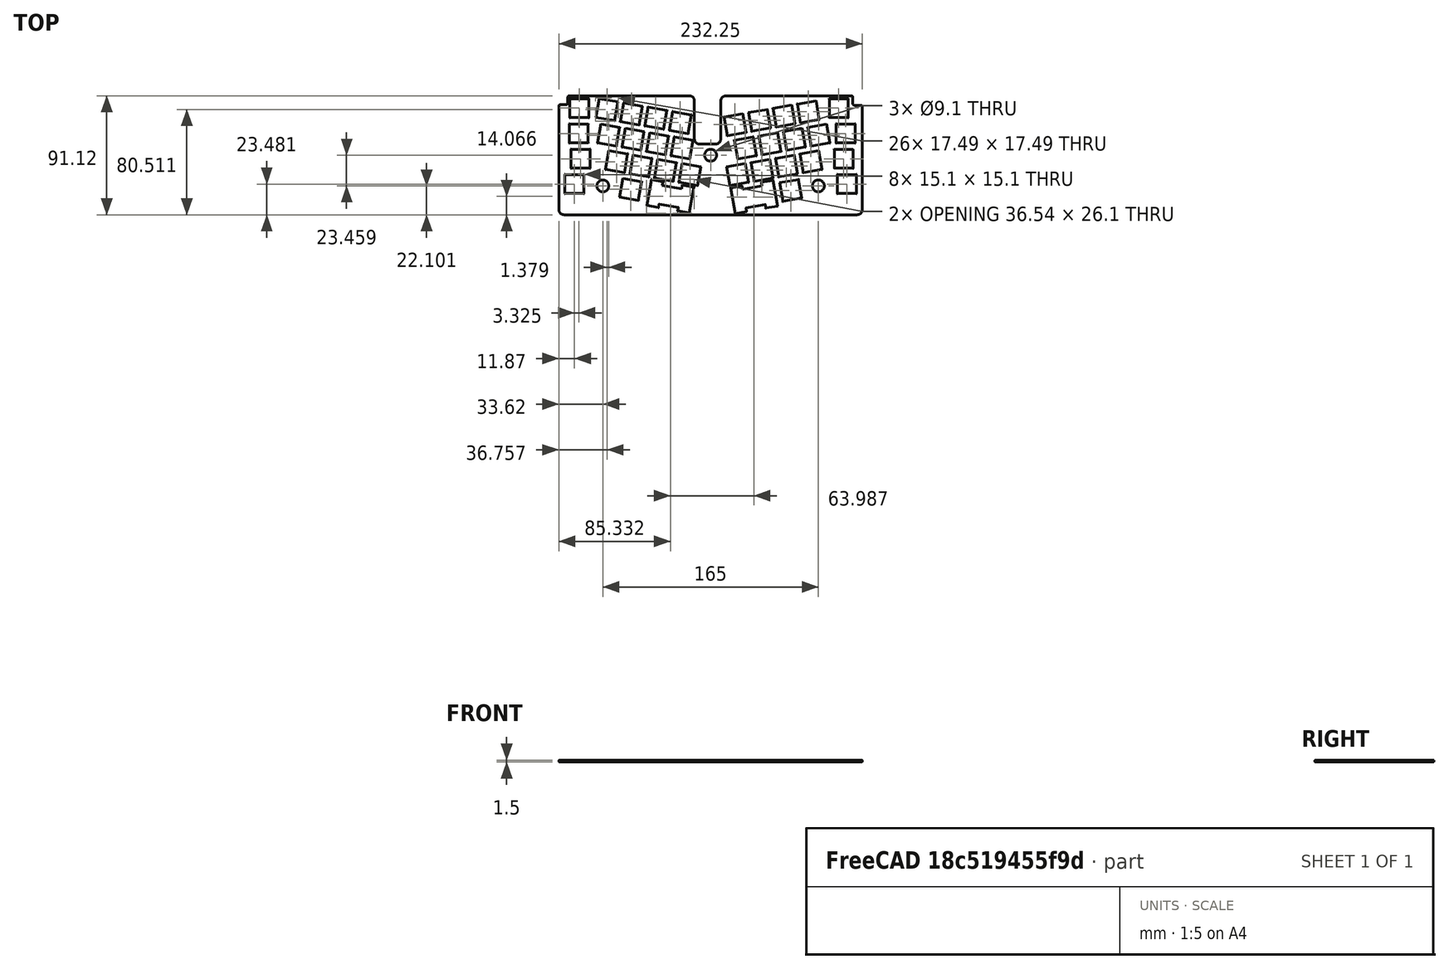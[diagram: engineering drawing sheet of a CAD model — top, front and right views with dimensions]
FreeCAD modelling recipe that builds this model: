
FCSTD DOCUMENT  (FreeCAD 0.20R)
Label: plate
License: All rights reserved
LicenseURL: http://en.wikipedia.org/wiki/All_rights_reserved
objects: Sketcher::SketchObject×1, PartDesign::Pad×1, PartDesign::Fillet×1, PartDesign::Body×1
note: 6 computed .brp shape members not serialized (recipe doc carries the construction recipe); baked Part::Feature solids carry a one-line shape summary decoded from their .brp

FEATURE [Sketcher::SketchObject] Sketch
  FullyConstrained = false
  sketch-geometry (187):
    g0: LineSegment StartX=-107.7 StartY=28.811 StartZ=0 EndX=-93.2 EndY=28.811 EndZ=0
    g1: LineSegment StartX=42.3215 StartY=-40.4517 StartZ=0 EndX=51.1237 EndY=-38.8997 EndZ=0
    g2: LineSegment StartX=27.5494 StartY=-43.0565 StartZ=0 EndX=18.7472 EndY=-44.6085 EndZ=0
    g3: LineSegment StartX=-25.1383 StartY=-42.644 StartZ=0 EndX=-16.3361 EndY=-44.1961 EndZ=0
    g4: LineSegment StartX=-48.7126 StartY=-38.4873 StartZ=0 EndX=-39.9104 EndY=-40.0393 EndZ=0
    g5: ArcOfCircle CenterX=112.125 CenterY=-41.561 CenterZ=0 NormalX=0 NormalY=0 NormalZ=1 AngleXU=0 Radius=4 StartAngle=4.71239 EndAngle=6.28319
    g6: LineSegment StartX=112.125 StartY=-45.561 StartZ=0 EndX=-112.125 EndY=-45.561 EndZ=0
    g7: ArcOfCircle CenterX=-112.125 CenterY=-41.561 CenterZ=0 NormalX=0 NormalY=0 NormalZ=1 AngleXU=0 Radius=4 StartAngle=3.14159 EndAngle=4.71239
    g8: Circle CenterX=-82.5 CenterY=-23.459 CenterZ=0 NormalX=0 NormalY=0 NormalZ=-1 AngleXU=0 Radius=4.55
    g9: Circle CenterX=0 CenterY=0 CenterZ=0 NormalX=0 NormalY=0 NormalZ=-1 AngleXU=0 Radius=4.55
    g10: Circle CenterX=82.5 CenterY=-23.459 CenterZ=0 NormalX=0 NormalY=0 NormalZ=-1 AngleXU=0 Radius=4.55
    g11: ArcOfCircle CenterX=110.225 CenterY=39.661 CenterZ=0 NormalX=0 NormalY=0 NormalZ=1 AngleXU=0 Radius=1.45 StartAngle=3.14159 EndAngle=4.71239
    g12: LineSegment StartX=115.125 StartY=38.211 StartZ=0 EndX=110.225 EndY=38.211 EndZ=0
    g13: LineSegment StartX=116.125 StartY=37.211 StartZ=0 EndX=116.125 EndY=-41.561 EndZ=0
    g14: ArcOfCircle CenterX=115.125 CenterY=37.211 CenterZ=0 NormalX=0 NormalY=0 NormalZ=1 AngleXU=0 Radius=1 StartAngle=0 EndAngle=1.5708
    g15: LineSegment StartX=108.775 StartY=44.561 StartZ=0 EndX=108.775 EndY=39.661 EndZ=0
    g16: ArcOfCircle CenterX=107.775 CenterY=44.561 CenterZ=0 NormalX=0 NormalY=0 NormalZ=1 AngleXU=0 Radius=1 StartAngle=0 EndAngle=1.5708
    g17: ArcOfCircle CenterX=-110.675 CenterY=40.111 CenterZ=0 NormalX=0 NormalY=0 NormalZ=1 AngleXU=0 Radius=1.45 StartAngle=4.71239 EndAngle=6.28319
    g18: LineSegment StartX=-109.225 StartY=44.561 StartZ=0 EndX=-109.225 EndY=40.111 EndZ=0
    g19: ArcOfCircle CenterX=-108.225 CenterY=44.561 CenterZ=0 NormalX=0 NormalY=0 NormalZ=1 AngleXU=0 Radius=1 StartAngle=1.5708 EndAngle=3.14159
    g20: LineSegment StartX=-115.125 StartY=38.661 StartZ=0 EndX=-110.675 EndY=38.661 EndZ=0
    g21: LineSegment StartX=-116.125 StartY=-41.561 StartZ=0 EndX=-116.125 EndY=37.661 EndZ=0
    g22: ArcOfCircle CenterX=-115.125 CenterY=37.661 CenterZ=0 NormalX=0 NormalY=0 NormalZ=1 AngleXU=0 Radius=1 StartAngle=1.5708 EndAngle=3.14159
    g23: LineSegment StartX=-16.4028 StartY=45.561 StartZ=0 EndX=-108.225 EndY=45.561 EndZ=0
    g24: ArcOfCircle CenterX=-16.4028 CenterY=41.561 CenterZ=0 NormalX=0 NormalY=0 NormalZ=1 AngleXU=0 Radius=4 StartAngle=0 EndAngle=1.5708
    g25: LineSegment StartX=11.7972 StartY=45.561 StartZ=0 EndX=107.775 EndY=45.561 EndZ=0
    g26: ArcOfCircle CenterX=11.7972 CenterY=41.561 CenterZ=0 NormalX=0 NormalY=0 NormalZ=1 AngleXU=0 Radius=4 StartAngle=1.5708 EndAngle=3.14159
    g27: LineSegment StartX=7.79716 StartY=12.541 StartZ=0 EndX=7.79716 EndY=41.561 EndZ=0
    g28: ArcOfCircle CenterX=3.79716 CenterY=12.541 CenterZ=0 NormalX=0 NormalY=0 NormalZ=1 AngleXU=0 Radius=4 StartAngle=4.71239 EndAngle=6.28319
    g29: LineSegment StartX=-8.40284 StartY=8.54105 StartZ=0 EndX=3.79716 EndY=8.54105 EndZ=0
    g30: LineSegment StartX=-12.4028 StartY=41.561 StartZ=0 EndX=-12.4028 EndY=12.541 EndZ=0
    g31: ArcOfCircle CenterX=-8.40284 CenterY=12.541 CenterZ=0 NormalX=0 NormalY=0 NormalZ=1 AngleXU=0 Radius=4 StartAngle=3.14159 EndAngle=4.71239
    g32: LineSegment StartX=68.8763 StartY=24.9023 StartZ=0 EndX=83.156 EndY=27.4202 EndZ=0
    g33: LineSegment StartX=68.8763 StartY=24.9023 StartZ=0 EndX=66.3584 EndY=39.1821 EndZ=0
    g34: LineSegment StartX=80.6381 StartY=41.6999 StartZ=0 EndX=83.156 EndY=27.4202 EndZ=0
    g35: LineSegment StartX=66.3584 StartY=39.1821 StartZ=0 EndX=80.6381 EndY=41.6999 EndZ=0
    g36: LineSegment StartX=50.165 StartY=21.603 StartZ=0 EndX=64.4447 EndY=24.1209 EndZ=0
    g37: LineSegment StartX=50.165 StartY=21.603 StartZ=0 EndX=47.6471 EndY=35.8827 EndZ=0
    g38: LineSegment StartX=61.9268 StartY=38.4006 StartZ=0 EndX=64.4447 EndY=24.1209 EndZ=0
    g39: LineSegment StartX=47.6471 StartY=35.8827 StartZ=0 EndX=61.9268 EndY=38.4006 EndZ=0
    g40: LineSegment StartX=31.4536 StartY=18.3037 StartZ=0 EndX=45.7333 EndY=20.8216 EndZ=0
    g41: LineSegment StartX=31.4536 StartY=18.3037 StartZ=0 EndX=28.9357 EndY=32.5834 EndZ=0
    g42: LineSegment StartX=43.2154 StartY=35.1013 StartZ=0 EndX=45.7333 EndY=20.8216 EndZ=0
    g43: LineSegment StartX=28.9357 StartY=32.5834 StartZ=0 EndX=43.2154 EndY=35.1013 EndZ=0
    g44: LineSegment StartX=12.7423 StartY=15.0044 StartZ=0 EndX=27.022 EndY=17.5223 EndZ=0
    g45: LineSegment StartX=12.7423 StartY=15.0044 StartZ=0 EndX=10.2244 EndY=29.2841 EndZ=0
    g46: LineSegment StartX=24.5041 StartY=31.802 StartZ=0 EndX=27.022 EndY=17.5223 EndZ=0
    g47: LineSegment StartX=10.2244 StartY=29.2841 StartZ=0 EndX=24.5041 EndY=31.802 EndZ=0
    g48: LineSegment StartX=20.7194 StartY=-2.88213 StartZ=0 EndX=34.9991 EndY=-0.364228 EndZ=0
    g49: LineSegment StartX=20.7194 StartY=-2.88213 StartZ=0 EndX=18.2015 EndY=11.3976 EndZ=0
    g50: LineSegment StartX=32.4812 StartY=13.9155 StartZ=0 EndX=34.9991 EndY=-0.364228 EndZ=0
    g51: LineSegment StartX=18.2015 StartY=11.3976 StartZ=0 EndX=32.4812 EndY=13.9155 EndZ=0
    g52: LineSegment StartX=39.4308 StartY=0.417189 StartZ=0 EndX=53.7105 EndY=2.93509 EndZ=0
    g53: LineSegment StartX=39.4308 StartY=0.417189 StartZ=0 EndX=36.9129 EndY=14.6969 EndZ=0
    g54: LineSegment StartX=51.1926 StartY=17.2148 StartZ=0 EndX=53.7105 EndY=2.93509 EndZ=0
    g55: LineSegment StartX=36.9129 StartY=14.6969 StartZ=0 EndX=51.1926 EndY=17.2148 EndZ=0
    g56: LineSegment StartX=58.1421 StartY=3.7165 StartZ=0 EndX=72.4218 EndY=6.2344 EndZ=0
    g57: LineSegment StartX=58.1421 StartY=3.7165 StartZ=0 EndX=55.6242 EndY=17.9962 EndZ=0
    g58: LineSegment StartX=69.9039 StartY=20.5141 StartZ=0 EndX=72.4218 EndY=6.2344 EndZ=0
    g59: LineSegment StartX=55.6242 StartY=17.9962 StartZ=0 EndX=69.9039 EndY=20.5141 EndZ=0
    g60: LineSegment StartX=76.8535 StartY=7.01582 StartZ=0 EndX=91.1332 EndY=9.53372 EndZ=0
    g61: LineSegment StartX=76.8535 StartY=7.01582 StartZ=0 EndX=74.3356 EndY=21.2955 EndZ=0
    g62: LineSegment StartX=88.6153 StartY=23.8134 StartZ=0 EndX=91.1332 EndY=9.53372 EndZ=0
    g63: LineSegment StartX=74.3356 StartY=21.2955 StartZ=0 EndX=88.6153 EndY=23.8134 EndZ=0
    g64: LineSegment StartX=70.7971 StartY=-13.3452 StartZ=0 EndX=85.0768 EndY=-10.8273 EndZ=0
    g65: LineSegment StartX=70.7971 StartY=-13.3452 StartZ=0 EndX=68.2792 EndY=0.934527 EndZ=0
    g66: LineSegment StartX=82.5589 StartY=3.45243 StartZ=0 EndX=85.0768 EndY=-10.8273 EndZ=0
    g67: LineSegment StartX=68.2792 StartY=0.934527 StartZ=0 EndX=82.5589 EndY=3.45243 EndZ=0
    g68: LineSegment StartX=52.0858 StartY=-16.6445 StartZ=0 EndX=66.3655 EndY=-14.1266 EndZ=0
    g69: LineSegment StartX=52.0858 StartY=-16.6445 StartZ=0 EndX=49.5679 EndY=-2.36479 EndZ=0
    g70: LineSegment StartX=63.8476 StartY=0.15311 StartZ=0 EndX=66.3655 EndY=-14.1266 EndZ=0
    g71: LineSegment StartX=49.5679 StartY=-2.36479 StartZ=0 EndX=63.8476 EndY=0.15311 EndZ=0
    g72: LineSegment StartX=33.3744 StartY=-19.9438 StartZ=0 EndX=47.6541 EndY=-17.4259 EndZ=0
    g73: LineSegment StartX=33.3744 StartY=-19.9438 StartZ=0 EndX=30.8565 EndY=-5.6641 EndZ=0
    g74: LineSegment StartX=45.1362 StartY=-3.14621 StartZ=0 EndX=47.6541 EndY=-17.4259 EndZ=0
    g75: LineSegment StartX=30.8565 StartY=-5.6641 StartZ=0 EndX=45.1362 EndY=-3.14621 EndZ=0
    g76: LineSegment StartX=14.6631 StartY=-23.2431 StartZ=0 EndX=28.9428 EndY=-20.7252 EndZ=0
    g77: LineSegment StartX=14.6631 StartY=-23.2431 StartZ=0 EndX=12.1452 EndY=-8.96342 EndZ=0
    g78: LineSegment StartX=26.4249 StartY=-6.44552 StartZ=0 EndX=28.9428 EndY=-20.7252 EndZ=0
    g79: LineSegment StartX=12.1452 StartY=-8.96342 StartZ=0 EndX=26.4249 EndY=-6.44552 EndZ=0
    g80: LineSegment StartX=27.0719 StartY=-40.3482 StartZ=0 EndX=41.844 EndY=-37.7435 EndZ=0
    g81: LineSegment StartX=41.844 StartY=-37.7435 StartZ=0 EndX=42.3215 EndY=-40.4517 EndZ=0
    g82: LineSegment StartX=27.0719 StartY=-40.3482 StartZ=0 EndX=27.5494 EndY=-43.0565 EndZ=0
    g83: LineSegment StartX=38.8485 StartY=-20.7556 StartZ=0 EndX=47.6508 EndY=-19.2035 EndZ=0
    g84: LineSegment StartX=51.1237 StartY=-38.8997 StartZ=0 EndX=47.6508 EndY=-19.2035 EndZ=0
    g85: LineSegment StartX=24.0764 StartY=-23.3603 StartZ=0 EndX=15.2742 EndY=-24.9124 EndZ=0
    g86: LineSegment StartX=18.7472 StartY=-44.6085 StartZ=0 EndX=15.2742 EndY=-24.9124 EndZ=0
    g87: LineSegment StartX=24.554 StartY=-26.0685 StartZ=0 EndX=24.0764 EndY=-23.3603 EndZ=0
    g88: LineSegment StartX=24.554 StartY=-26.0685 StartZ=0 EndX=39.3261 EndY=-23.4638 EndZ=0
    g89: LineSegment StartX=39.3261 StartY=-23.4638 StartZ=0 EndX=38.8485 EndY=-20.7556 EndZ=0
    g90: LineSegment StartX=90.825 StartY=43.311 StartZ=0 EndX=90.825 EndY=28.811 EndZ=0
    g91: LineSegment StartX=90.825 StartY=43.311 StartZ=0 EndX=105.325 EndY=43.311 EndZ=0
    g92: LineSegment StartX=90.825 StartY=28.811 StartZ=0 EndX=105.325 EndY=28.811 EndZ=0
    g93: LineSegment StartX=105.325 StartY=43.311 StartZ=0 EndX=105.325 EndY=28.811 EndZ=0
    g94: LineSegment StartX=110.55 StartY=23.931 StartZ=0 EndX=110.55 EndY=9.43101 EndZ=0
    g95: LineSegment StartX=96.05 StartY=9.43101 StartZ=0 EndX=110.55 EndY=9.43101 EndZ=0
    g96: LineSegment StartX=96.05 StartY=23.931 StartZ=0 EndX=110.55 EndY=23.931 EndZ=0
    g97: LineSegment StartX=96.05 StartY=23.931 StartZ=0 EndX=96.05 EndY=9.43101 EndZ=0
    g98: LineSegment StartX=109.125 StartY=4.55101 StartZ=0 EndX=109.125 EndY=-9.94899 EndZ=0
    g99: LineSegment StartX=94.625 StartY=-9.94899 StartZ=0 EndX=109.125 EndY=-9.94899 EndZ=0
    g100: LineSegment StartX=94.625 StartY=4.55101 StartZ=0 EndX=109.125 EndY=4.55101 EndZ=0
    g101: LineSegment StartX=94.625 StartY=4.55101 StartZ=0 EndX=94.625 EndY=-9.94899 EndZ=0
    g102: LineSegment StartX=111.5 StartY=-14.829 StartZ=0 EndX=111.5 EndY=-29.329 EndZ=0
    g103: LineSegment StartX=97 StartY=-29.329 StartZ=0 EndX=111.5 EndY=-29.329 EndZ=0
    g104: LineSegment StartX=97 StartY=-14.829 StartZ=0 EndX=111.5 EndY=-14.829 EndZ=0
    g105: LineSegment StartX=97 StartY=-14.829 StartZ=0 EndX=97 EndY=-29.329 EndZ=0
    g106: LineSegment StartX=52.8672 StartY=-21.0761 StartZ=0 EndX=67.1469 EndY=-18.5582 EndZ=0
    g107: LineSegment StartX=67.1469 StartY=-18.5582 StartZ=0 EndX=69.6648 EndY=-32.8379 EndZ=0
    g108: LineSegment StartX=55.3851 StartY=-35.3558 StartZ=0 EndX=52.8672 EndY=-21.0761 EndZ=0
    g109: LineSegment StartX=55.3851 StartY=-35.3558 StartZ=0 EndX=69.6648 EndY=-32.8379 EndZ=0
    g110: LineSegment StartX=-85.2438 StartY=43.3496 StartZ=0 EndX=-87.7617 EndY=29.0699 EndZ=0
    g111: LineSegment StartX=-85.2438 StartY=43.3496 StartZ=0 EndX=-70.9641 EndY=40.8317 EndZ=0
    g112: LineSegment StartX=-87.7617 StartY=29.0699 StartZ=0 EndX=-73.482 EndY=26.552 EndZ=0
    g113: LineSegment StartX=-70.9641 StartY=40.8317 StartZ=0 EndX=-73.482 EndY=26.552 EndZ=0
    g114: LineSegment StartX=-66.5325 StartY=40.0503 StartZ=0 EndX=-69.0504 EndY=25.7706 EndZ=0
    g115: LineSegment StartX=-66.5325 StartY=40.0503 StartZ=0 EndX=-52.2528 EndY=37.5324 EndZ=0
    g116: LineSegment StartX=-69.0504 StartY=25.7706 StartZ=0 EndX=-54.7707 EndY=23.2527 EndZ=0
    g117: LineSegment StartX=-52.2528 StartY=37.5324 StartZ=0 EndX=-54.7707 EndY=23.2527 EndZ=0
    g118: LineSegment StartX=-47.8211 StartY=36.751 StartZ=0 EndX=-50.339 EndY=22.4713 EndZ=0
    g119: LineSegment StartX=-47.8211 StartY=36.751 StartZ=0 EndX=-33.5414 EndY=34.2331 EndZ=0
    g120: LineSegment StartX=-50.339 StartY=22.4713 StartZ=0 EndX=-36.0593 EndY=19.9534 EndZ=0
    g121: LineSegment StartX=-33.5414 StartY=34.2331 StartZ=0 EndX=-36.0593 EndY=19.9534 EndZ=0
    g122: LineSegment StartX=-29.1098 StartY=33.4517 StartZ=0 EndX=-31.6277 EndY=19.1719 EndZ=0
    g123: LineSegment StartX=-29.1098 StartY=33.4517 StartZ=0 EndX=-14.8301 EndY=30.9338 EndZ=0
    g124: LineSegment StartX=-31.6277 StartY=19.1719 StartZ=0 EndX=-17.348 EndY=16.654 EndZ=0
    g125: LineSegment StartX=-14.8301 StartY=30.9338 StartZ=0 EndX=-17.348 EndY=16.654 EndZ=0
    g126: LineSegment StartX=-83.8653 StartY=23.8134 StartZ=0 EndX=-86.3832 EndY=9.53372 EndZ=0
    g127: LineSegment StartX=-83.8653 StartY=23.8134 StartZ=0 EndX=-69.5856 EndY=21.2955 EndZ=0
    g128: LineSegment StartX=-86.3832 StartY=9.53372 StartZ=0 EndX=-72.1035 EndY=7.01582 EndZ=0
    g129: LineSegment StartX=-69.5856 StartY=21.2955 StartZ=0 EndX=-72.1035 EndY=7.01582 EndZ=0
    g130: LineSegment StartX=-65.1539 StartY=20.5141 StartZ=0 EndX=-67.6718 EndY=6.2344 EndZ=0
    g131: LineSegment StartX=-65.1539 StartY=20.5141 StartZ=0 EndX=-50.8742 EndY=17.9962 EndZ=0
    g132: LineSegment StartX=-67.6718 StartY=6.2344 StartZ=0 EndX=-53.3921 EndY=3.7165 EndZ=0
    g133: LineSegment StartX=-50.8742 StartY=17.9962 StartZ=0 EndX=-53.3921 EndY=3.7165 EndZ=0
    g134: LineSegment StartX=-46.4426 StartY=17.2148 StartZ=0 EndX=-48.9605 EndY=2.93509 EndZ=0
    g135: LineSegment StartX=-46.4426 StartY=17.2148 StartZ=0 EndX=-32.1629 EndY=14.6969 EndZ=0
    g136: LineSegment StartX=-48.9605 StartY=2.93509 StartZ=0 EndX=-34.6808 EndY=0.417189 EndZ=0
    g137: LineSegment StartX=-32.1629 StartY=14.6969 StartZ=0 EndX=-34.6808 EndY=0.417189 EndZ=0
    g138: LineSegment StartX=-27.7312 StartY=13.9155 StartZ=0 EndX=-30.2491 EndY=-0.364228 EndZ=0
    g139: LineSegment StartX=-27.7312 StartY=13.9155 StartZ=0 EndX=-13.4515 EndY=11.3976 EndZ=0
    g140: LineSegment StartX=-30.2491 StartY=-0.364228 StartZ=0 EndX=-15.9694 EndY=-2.88213 EndZ=0
    g141: LineSegment StartX=-13.4515 StartY=11.3976 StartZ=0 EndX=-15.9694 EndY=-2.88213 EndZ=0
    g142: LineSegment StartX=-77.8089 StartY=3.45243 StartZ=0 EndX=-80.3268 EndY=-10.8273 EndZ=0
    g143: LineSegment StartX=-77.8089 StartY=3.45243 StartZ=0 EndX=-63.5292 EndY=0.934527 EndZ=0
    g144: LineSegment StartX=-80.3268 StartY=-10.8273 StartZ=0 EndX=-66.0471 EndY=-13.3452 EndZ=0
    g145: LineSegment StartX=-63.5292 StartY=0.934527 StartZ=0 EndX=-66.0471 EndY=-13.3452 EndZ=0
    g146: LineSegment StartX=-59.0976 StartY=0.15311 StartZ=0 EndX=-61.6155 EndY=-14.1266 EndZ=0
    g147: LineSegment StartX=-59.0976 StartY=0.15311 StartZ=0 EndX=-44.8179 EndY=-2.36479 EndZ=0
    g148: LineSegment StartX=-61.6155 StartY=-14.1266 StartZ=0 EndX=-47.3358 EndY=-16.6445 EndZ=0
    g149: LineSegment StartX=-44.8179 StartY=-2.36479 StartZ=0 EndX=-47.3358 EndY=-16.6445 EndZ=0
    g150: LineSegment StartX=-40.3862 StartY=-3.14621 StartZ=0 EndX=-42.9041 EndY=-17.4259 EndZ=0
    g151: LineSegment StartX=-40.3862 StartY=-3.14621 StartZ=0 EndX=-26.1065 EndY=-5.6641 EndZ=0
    g152: LineSegment StartX=-42.9041 StartY=-17.4259 StartZ=0 EndX=-28.6244 EndY=-19.9438 EndZ=0
    g153: LineSegment StartX=-26.1065 StartY=-5.6641 StartZ=0 EndX=-28.6244 EndY=-19.9438 EndZ=0
    g154: LineSegment StartX=-21.6749 StartY=-6.44552 StartZ=0 EndX=-24.1928 EndY=-20.7252 EndZ=0
    g155: LineSegment StartX=-21.6749 StartY=-6.44552 StartZ=0 EndX=-7.39518 EndY=-8.96342 EndZ=0
    g156: LineSegment StartX=-24.1928 StartY=-20.7252 StartZ=0 EndX=-9.91308 EndY=-23.2431 EndZ=0
    g157: LineSegment StartX=-7.39518 StartY=-8.96342 StartZ=0 EndX=-9.91308 EndY=-23.2431 EndZ=0
    g158: LineSegment StartX=-67.0747 StartY=-17.7334 StartZ=0 EndX=-69.5926 EndY=-32.0131 EndZ=0
    g159: LineSegment StartX=-67.0747 StartY=-17.7334 StartZ=0 EndX=-52.795 EndY=-20.2513 EndZ=0
    g160: LineSegment StartX=-69.5926 StartY=-32.0131 StartZ=0 EndX=-55.3129 EndY=-34.531 EndZ=0
    g161: LineSegment StartX=-52.795 StartY=-20.2513 StartZ=0 EndX=-55.3129 EndY=-34.531 EndZ=0
    g162: LineSegment StartX=-24.6608 StartY=-39.9358 StartZ=0 EndX=-25.1383 EndY=-42.644 EndZ=0
    g163: LineSegment StartX=-39.4329 StartY=-37.3311 StartZ=0 EndX=-24.6608 EndY=-39.9358 EndZ=0
    g164: LineSegment StartX=-39.9104 StartY=-40.0393 StartZ=0 EndX=-39.4329 EndY=-37.3311 EndZ=0
    g165: LineSegment StartX=-45.2397 StartY=-18.7911 StartZ=0 EndX=-36.4375 EndY=-20.3432 EndZ=0
    g166: LineSegment StartX=-45.2397 StartY=-18.7911 StartZ=0 EndX=-48.7126 EndY=-38.4873 EndZ=0
    g167: LineSegment StartX=-36.4375 StartY=-20.3432 StartZ=0 EndX=-36.915 EndY=-23.0514 EndZ=0
    g168: LineSegment StartX=-22.1429 StartY=-25.6561 StartZ=0 EndX=-21.6654 EndY=-22.9479 EndZ=0
    g169: LineSegment StartX=-36.915 StartY=-23.0514 StartZ=0 EndX=-22.1429 EndY=-25.6561 EndZ=0
    g170: LineSegment StartX=-21.6654 StartY=-22.9479 StartZ=0 EndX=-12.8631 EndY=-24.5 EndZ=0
    g171: LineSegment StartX=-16.3361 StartY=-44.1961 StartZ=0 EndX=-12.8631 EndY=-24.5 EndZ=0
    g172: LineSegment StartX=-111.5 StartY=-14.829 StartZ=0 EndX=-97 EndY=-14.829 EndZ=0
    g173: LineSegment StartX=-111.5 StartY=-14.829 StartZ=0 EndX=-111.5 EndY=-29.329 EndZ=0
    g174: LineSegment StartX=-97 StartY=-14.829 StartZ=0 EndX=-97 EndY=-29.329 EndZ=0
    g175: LineSegment StartX=-111.5 StartY=-29.329 StartZ=0 EndX=-97 EndY=-29.329 EndZ=0
    g176: LineSegment StartX=-106.75 StartY=4.55101 StartZ=0 EndX=-92.25 EndY=4.55101 EndZ=0
    g177: LineSegment StartX=-106.75 StartY=4.55101 StartZ=0 EndX=-106.75 EndY=-9.94899 EndZ=0
    g178: LineSegment StartX=-92.25 StartY=4.55101 StartZ=0 EndX=-92.25 EndY=-9.94899 EndZ=0
    g179: LineSegment StartX=-106.75 StartY=-9.94899 StartZ=0 EndX=-92.25 EndY=-9.94899 EndZ=0
    g180: LineSegment StartX=-108.175 StartY=23.931 StartZ=0 EndX=-93.675 EndY=23.931 EndZ=0
    g181: LineSegment StartX=-108.175 StartY=23.931 StartZ=0 EndX=-108.175 EndY=9.43101 EndZ=0
    g182: LineSegment StartX=-93.675 StartY=23.931 StartZ=0 EndX=-93.675 EndY=9.43101 EndZ=0
    g183: LineSegment StartX=-108.175 StartY=9.43101 StartZ=0 EndX=-93.675 EndY=9.43101 EndZ=0
    g184: LineSegment StartX=-107.7 StartY=43.311 StartZ=0 EndX=-93.2 EndY=43.311 EndZ=0
    g185: LineSegment StartX=-107.7 StartY=43.311 StartZ=0 EndX=-107.7 EndY=28.811 EndZ=0
    g186: LineSegment StartX=-93.2 StartY=43.311 StartZ=0 EndX=-93.2 EndY=28.811 EndZ=0
  constraints (184):
    c: Coincident(g7,g21)
    c: Coincident(g21,g22)
    c: Coincident(g20,g22)
    c: Coincident(g6,g7)
    c: Coincident(g173,g175)
    c: Coincident(g172,g173)
    c: Coincident(g17,g20)
    c: Coincident(g17,g18)
    c: Coincident(g18,g19)
    c: Coincident(g19,g23)
    c: Coincident(g181,g183)
    c: Coincident(g180,g181)
    c: Coincident(g0,g185)
    c: Coincident(g184,g185)
    c: Coincident(g177,g179)
    c: Coincident(g176,g177)
    c: Coincident(g174,g175)
    c: Coincident(g172,g174)
    c: Coincident(g182,g183)
    c: Coincident(g180,g182)
    c: Coincident(g0,g186)
    c: Coincident(g184,g186)
    c: Coincident(g178,g179)
    c: Coincident(g176,g178)
    c: Coincident(g110,g112)
    c: Coincident(g126,g128)
    c: Coincident(g110,g111)
    c: Coincident(g126,g127)
    c: Coincident(g142,g144)
    c: Coincident(g142,g143)
    c: Coincident(g112,g113)
    c: Coincident(g128,g129)
    c: Coincident(g111,g113)
    c: Coincident(g158,g160)
    c: Coincident(g127,g129)
    c: Coincident(g114,g116)
    c: Coincident(g130,g132)
    c: Coincident(g158,g159)
    c: Coincident(g114,g115)
    c: Coincident(g144,g145)
    c: Coincident(g130,g131)
    c: Coincident(g143,g145)
    c: Coincident(g146,g148)
    c: Coincident(g146,g147)
    c: Coincident(g160,g161)
    c: Coincident(g116,g117)
    c: Coincident(g132,g133)
    c: Coincident(g159,g161)
    c: Coincident(g115,g117)
    c: Coincident(g131,g133)
    c: Coincident(g118,g120)
    c: Coincident(g134,g136)
    c: Coincident(g4,g166)
    c: Coincident(g118,g119)
    c: Coincident(g148,g149)
    c: Coincident(g134,g135)
    c: Coincident(g165,g166)
    c: Coincident(g147,g149)
    c: Coincident(g150,g152)
    c: Coincident(g150,g151)
    c: Coincident(g4,g164)
    c: Coincident(g163,g164)
    c: Coincident(g167,g169)
    c: Coincident(g165,g167)
    c: Coincident(g120,g121)
    c: Coincident(g136,g137)
    c: Coincident(g119,g121)
    c: Coincident(g135,g137)
    c: Coincident(g122,g124)
    c: Coincident(g138,g140)
    c: Coincident(g122,g123)
    c: Coincident(g152,g153)
    c: Coincident(g138,g139)
    c: Coincident(g151,g153)
    c: Coincident(g3,g162)
    c: Coincident(g162,g163)
    c: Coincident(g154,g156)
    c: Coincident(g168,g169)
    c: Coincident(g154,g155)
    c: Coincident(g168,g170)
    c: Coincident(g124,g125)
    c: Coincident(g23,g24)
    c: Coincident(g3,g171)
    c: Coincident(g140,g141)
    c: Coincident(g123,g125)
    c: Coincident(g139,g141)
    c: Coincident(g170,g171)
    c: Coincident(g30,g31)
    c: Coincident(g24,g30)
    c: Coincident(g156,g157)
    c: Coincident(g29,g31)
    c: Coincident(g155,g157)
    c: Coincident(g28,g29)
    c: Coincident(g27,g28)
    c: Coincident(g26,g27)
    c: Coincident(g45,g47)
    c: Coincident(g25,g26)
    c: Coincident(g77,g79)
    c: Coincident(g44,g45)
    c: Coincident(g76,g77)
    c: Coincident(g85,g86)
    c: Coincident(g49,g51)
    c: Coincident(g2,g86)
    c: Coincident(g48,g49)
    c: Coincident(g85,g87)
    c: Coincident(g46,g47)
    c: Coincident(g87,g88)
    c: Coincident(g78,g79)
    c: Coincident(g44,g46)
    c: Coincident(g80,g82)
    c: Coincident(g2,g82)
    c: Coincident(g41,g43)
    c: Coincident(g76,g78)
    c: Coincident(g73,g75)
    c: Coincident(g40,g41)
    c: Coincident(g50,g51)
    c: Coincident(g72,g73)
    c: Coincident(g48,g50)
    c: Coincident(g53,g55)
    c: Coincident(g83,g89)
    c: Coincident(g88,g89)
    c: Coincident(g52,g53)
    c: Coincident(g80,g81)
    c: Coincident(g1,g81)
    c: Coincident(g42,g43)
    c: Coincident(g74,g75)
    c: Coincident(g40,g42)
    c: Coincident(g37,g39)
    c: Coincident(g83,g84)
    c: Coincident(g72,g74)
    c: Coincident(g69,g71)
    c: Coincident(g36,g37)
    c: Coincident(g1,g84)
    c: Coincident(g54,g55)
    c: Coincident(g68,g69)
    c: Coincident(g106,g108)
    c: Coincident(g52,g54)
    c: Coincident(g108,g109)
    c: Coincident(g57,g59)
    c: Coincident(g56,g57)
    c: Coincident(g38,g39)
    c: Coincident(g70,g71)
    c: Coincident(g36,g38)
    c: Coincident(g33,g35)
    c: Coincident(g68,g70)
    c: Coincident(g106,g107)
    c: Coincident(g65,g67)
    c: Coincident(g32,g33)
    c: Coincident(g107,g109)
    c: Coincident(g58,g59)
    c: Coincident(g64,g65)
    c: Coincident(g56,g58)
    c: Coincident(g61,g63)
    c: Coincident(g60,g61)
    c: Coincident(g34,g35)
    c: Coincident(g66,g67)
    c: Coincident(g32,g34)
    c: Coincident(g64,g66)
    c: Coincident(g62,g63)
    c: Coincident(g90,g92)
    c: Coincident(g90,g91)
    c: Coincident(g60,g62)
    c: Coincident(g99,g101)
    c: Coincident(g100,g101)
    c: Coincident(g95,g97)
    c: Coincident(g96,g97)
    c: Coincident(g103,g105)
    c: Coincident(g104,g105)
    c: Coincident(g92,g93)
    c: Coincident(g91,g93)
    c: Coincident(g16,g25)
    c: Coincident(g11,g15)
    c: Coincident(g15,g16)
    c: Coincident(g98,g99)
    c: Coincident(g98,g100)
    c: Coincident(g11,g12)
    c: Coincident(g94,g95)
    c: Coincident(g94,g96)
    c: Coincident(g102,g103)
    c: Coincident(g102,g104)
    c: Coincident(g5,g6)
    c: Coincident(g12,g14)
    c: Coincident(g5,g13)
    c: Coincident(g13,g14)
FEATURE [PartDesign::Pad] Pad
  Direction = (0,0,1)
  Length = 1.5
  Length2 = 10
  Profile = -> Sketch
  ReferenceAxis = -> Sketch [N_Axis]
  Type = 0
FEATURE [PartDesign::Fillet] Fillet
  Base = -> Pad [Face189,Face188]
  BaseFeature = -> Pad
  Radius = 0.3
  SupportTransform = false
  UseAllEdges = false
FEATURE [PartDesign::Body] Body
  Group = -> [Sketch,Pad,Fillet]
  Origin = -> Origin
  Tip = -> Fillet
